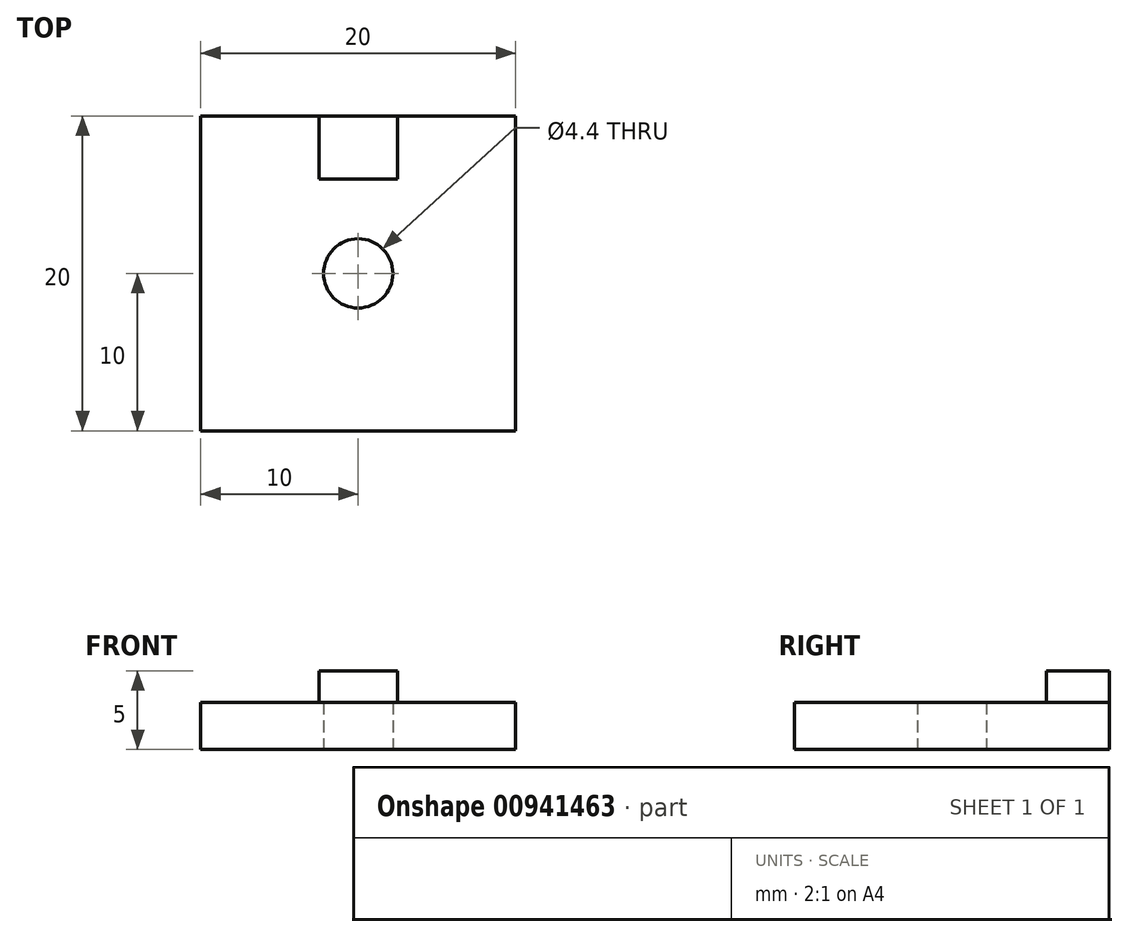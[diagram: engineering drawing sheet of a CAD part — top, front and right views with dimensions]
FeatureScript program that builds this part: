
annotation { "Feature Type Name" : "Feature", "Feature Type Description" : "" }
export const myFeature = defineFeature(function(context is Context, id is Id, definition is map)
    precondition{}
    {
        {
            var Q0;
            Q0=qCreatedBy(makeId("Top.planeOp"),FACE);
            var sketch = newSketch(context, id + "F0", { "sketchPlane" : qUnion([Q0])});
            skLineSegment(sketch, "E0.bottom", {"start": v(10, -10) * mm, "end": v(-10, -10) * mm});
            skLineSegment(sketch, "E0.top", {"start": v(10, 10) * mm, "end": v(-10, 10) * mm});
            skLineSegment(sketch, "E0.left", {"start": v(10, -10) * mm, "end": v(10, 10) * mm});
            skLineSegment(sketch, "E0.right", {"start": v(-10, -10) * mm, "end": v(-10, 10) * mm});
            skPoint(sketch, "E0.middle", {"position": v(0, 0) * mm});
            skCircle(sketch, "E1", {"center": v(0, 0) * mm, "radius": 2.2 * mm});
            skSolve(sketch);
        }
        {
            var Q0;
            Q0=makeQuery(id+"F0.imprint","IMPRINT",FACE,{"disambiguationData":[TD([[makeQuery(id+"F0.imprint","IMPRINT",EDGE,{"derivedFrom":sQuery(id+"F0.wireOp",EDGE,"E0.bottom")}),-1.0]])]});
            extrude(context, id + "F1", {"entities" : qUnion([Q0]), "depth" : 3 * mm, "offsetDistance" : 25 * mm});
        }
        {
            var Q0;
            Q0=makeQuery(id+"F1.opExtrude","CAP_FACE",FACE,{"disambiguationData":[OSD([sQuery(id+"F0.wireOp",EDGE,"E0.bottom"),sQuery(id+"F0.wireOp",EDGE,"E0.top"),sQuery(id+"F0.wireOp",EDGE,"E0.left"),sQuery(id+"F0.wireOp",EDGE,"E0.right"),sQuery(id+"F0.wireOp",EDGE,"E1")])],"isStart":false});
            var sketch = newSketch(context, id + "F2", { "sketchPlane" : qUnion([Q0])});
            skLineSegment(sketch, "E2.bottom", {"start": v(-2.5, 10) * mm, "end": v(2.5, 10) * mm});
            skLineSegment(sketch, "E2.top", {"start": v(-2.5, 6) * mm, "end": v(2.5, 6) * mm});
            skLineSegment(sketch, "E2.left", {"start": v(-2.5, 10) * mm, "end": v(-2.5, 6) * mm});
            skLineSegment(sketch, "E2.right", {"start": v(2.5, 10) * mm, "end": v(2.5, 6) * mm});
            skSolve(sketch);
        }
        {
            var Q0;
            Q0=makeQuery(id+"F2.imprint","IMPRINT",FACE,{"disambiguationData":[TD([[makeQuery(id+"F2.imprint","IMPRINT",EDGE,{"derivedFrom":sQuery(id+"F2.wireOp",EDGE,"E2.bottom")}),1.0]])]});
            extrude(context, id + "F3", {"entities" : qUnion([Q0]), "operationType" : NewBodyOperationType.ADD, "depth" : 2 * mm, "offsetDistance" : 25 * mm});
        }
    });
